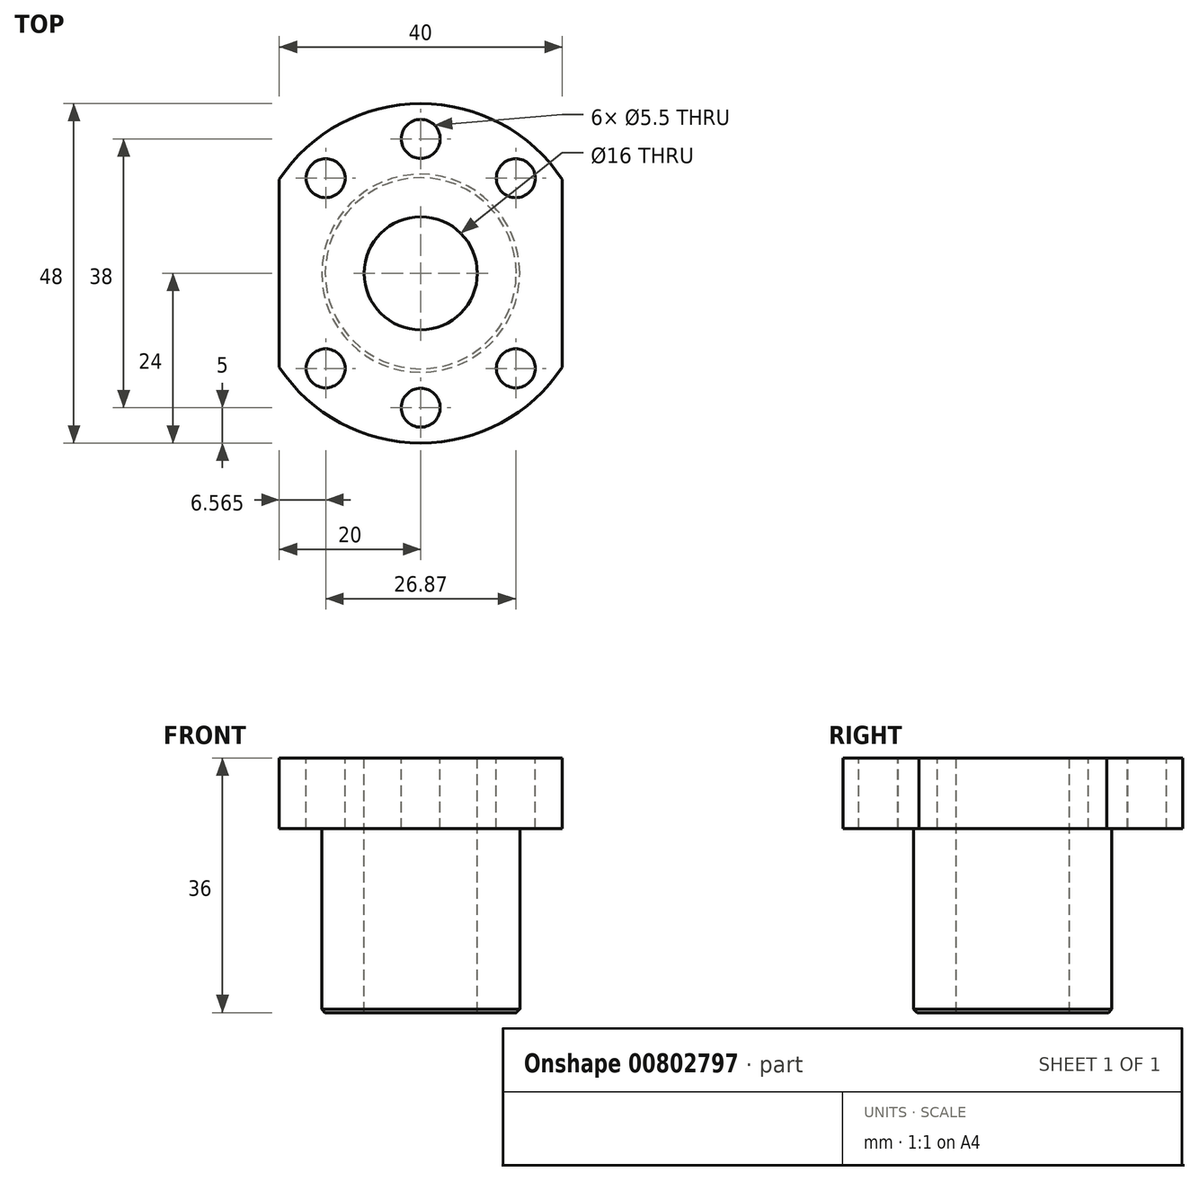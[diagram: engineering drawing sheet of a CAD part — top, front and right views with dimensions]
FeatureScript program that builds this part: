
annotation { "Feature Type Name" : "Feature", "Feature Type Description" : "" }
export const myFeature = defineFeature(function(context is Context, id is Id, definition is map)
    precondition{}
    {
        {
            var Q0;
            Q0=qCreatedBy(makeId("Top.planeOp"),FACE);
            var sketch = newSketch(context, id + "F0", { "sketchPlane" : qUnion([Q0])});
            skCircle(sketch, "E0", {"center": v(0, 0) * mm, "radius": 24 * mm});
            skCircle(sketch, "E1", {"center": v(0, 0) * mm, "radius": 14 * mm});
            skCircle(sketch, "E2", {"center": v(0, 0) * mm, "radius": 8 * mm});
            skLineSegment(sketch, "E3", {"start": v(-20, 29.43) * mm, "end": v(-20, -27.45) * mm});
            skLineSegment(sketch, "E4", {"start": v(20, 27.86) * mm, "end": v(20, -28.8) * mm});
            skLineSegment(sketch, "E5", {"start": v(0, 0) * mm, "end": v(-20, 0) * mm, "construction": true});
            skLineSegment(sketch, "E6", {"start": v(0, 0) * mm, "end": v(20, 0) * mm, "construction": true});
            skCircle(sketch, "E7", {"center": v(0, 0) * mm, "radius": 19 * mm, "construction": true});
            skLineSegment(sketch, "E8.rect.bottom", {"start": v(13.44, 13.44) * mm, "end": v(-13.44, 13.44) * mm, "construction": true});
            skLineSegment(sketch, "E8.rect.top", {"start": v(13.44, -13.44) * mm, "end": v(-13.44, -13.44) * mm, "construction": true});
            skLineSegment(sketch, "E8.rect.left", {"start": v(13.44, 13.44) * mm, "end": v(13.44, -13.44) * mm, "construction": true});
            skLineSegment(sketch, "E8.rect.right", {"start": v(-13.44, 13.44) * mm, "end": v(-13.44, -13.44) * mm, "construction": true});
            skCircle(sketch, "E9", {"center": v(-13.44, 13.44) * mm, "radius": 2.75 * mm});
            skCircle(sketch, "E10", {"center": v(0, 19) * mm, "radius": 2.75 * mm});
            skPoint(sketch, "E10.centerSnap0", {"position": v(0, 13.44) * mm});
            skCircle(sketch, "E11", {"center": v(13.44, 13.44) * mm, "radius": 2.75 * mm});
            skCircle(sketch, "E12", {"center": v(13.44, -13.44) * mm, "radius": 2.75 * mm});
            skCircle(sketch, "E13", {"center": v(-13.44, -13.44) * mm, "radius": 2.75 * mm});
            skCircle(sketch, "E14", {"center": v(0, -19) * mm, "radius": 2.75 * mm});
            skSolve(sketch);
        }
        {
            var Q0;
            Q0=makeQuery(id+"F0.imprint","IMPRINT",FACE,{"disambiguationData":[TD([[makeQuery(id+"F0.imprint","IMPRINT",EDGE,{"derivedFrom":sQuery(id+"F0.wireOp",EDGE,"E1")}),-1.0]])]});
            var Q1;
            Q1=makeQuery(id+"F0.imprint","IMPRINT",FACE,{"disambiguationData":[TD([[makeQuery(id+"F0.imprint","IMPRINT",EDGE,{"derivedFrom":sQuery(id+"F0.wireOp",EDGE,"E1")}),1.0]])]});
            extrude(context, id + "F1", {"entities" : qUnion([Q0, Q1]), "oppositeDirection" : true, "depth" : 10 * mm});
        }
        {
            var Q0;
            Q0=makeQuery(id+"F0.imprint","IMPRINT",FACE,{"disambiguationData":[TD([[makeQuery(id+"F0.imprint","IMPRINT",EDGE,{"derivedFrom":sQuery(id+"F0.wireOp",EDGE,"E1")}),1.0]])]});
            extrude(context, id + "F2", {"entities" : qUnion([Q0]), "operationType" : NewBodyOperationType.ADD, "oppositeDirection" : true, "depth" : 36 * mm});
        }
        {
            var Q0;
            Q0=makeQuery(id+"F2.opExtrude","CAP_EDGE",EDGE,{"disambiguationData":[OSD([sQuery(id+"F0.wireOp",EDGE,"E1")])],"isStart":false});
            chamfer(context, id + "F3", {"entities" : qUnion([Q0]), "width" : .5 * mm, "tangentPropagation" : true});
        }
    });
